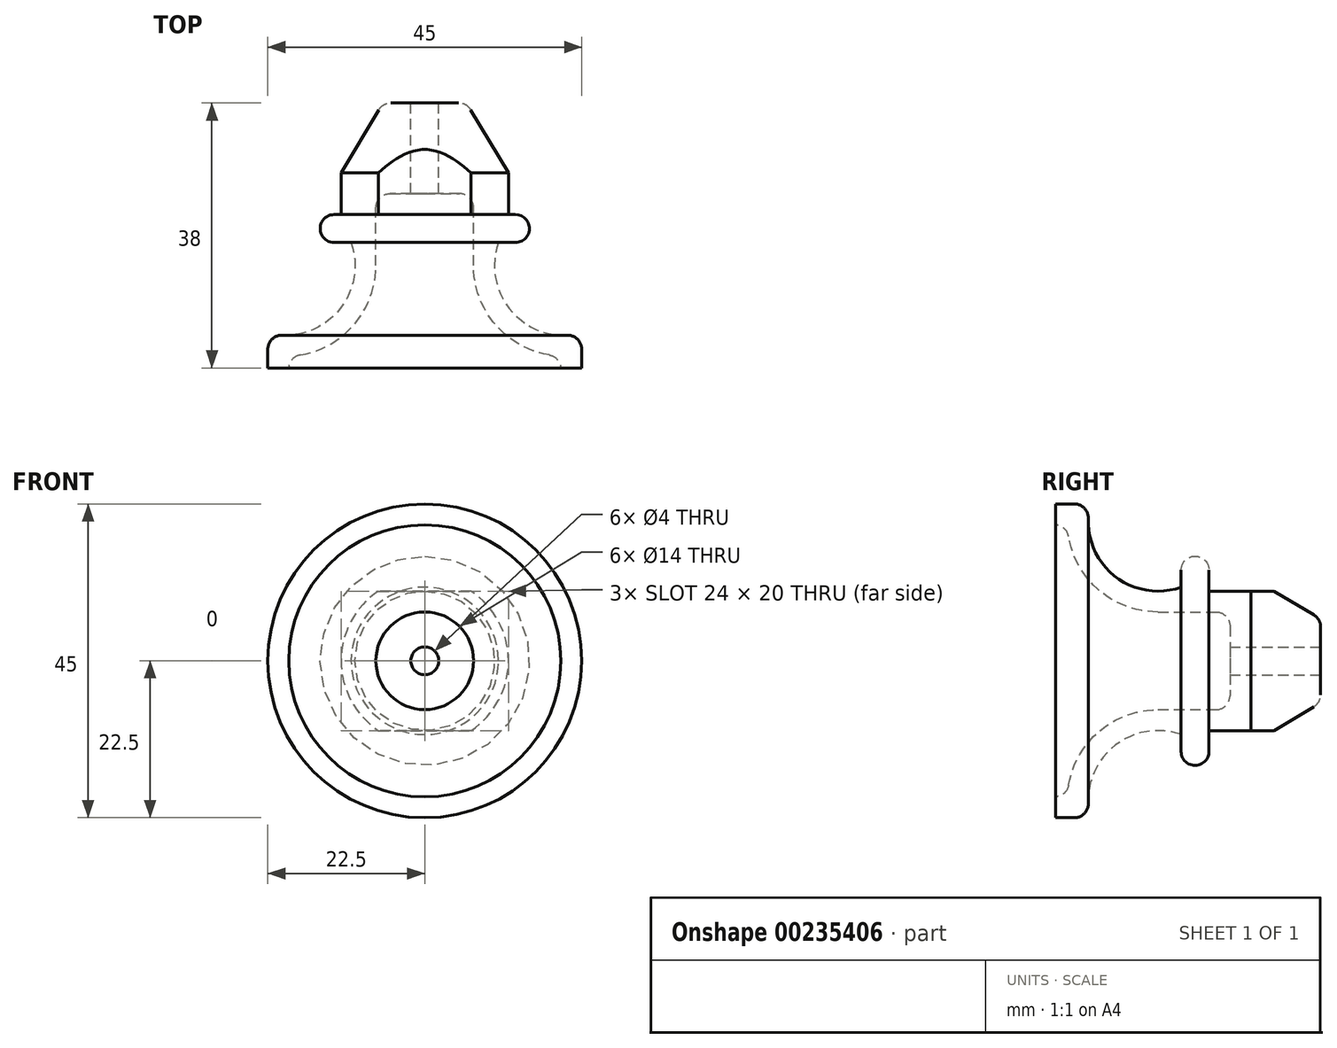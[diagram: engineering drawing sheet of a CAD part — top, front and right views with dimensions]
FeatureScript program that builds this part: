
annotation { "Feature Type Name" : "Feature", "Feature Type Description" : "" }
export const myFeature = defineFeature(function(context is Context, id is Id, definition is map)
    precondition{}
    {
        {
            var Q0;
            Q0=qCreatedBy(makeId("Top.planeOp"),FACE);
            var sketch = newSketch(context, id + "F0", { "sketchPlane" : qUnion([Q0])});
            skLineSegment(sketch, "E0", {"start": v(0, 22.95) * mm, "end": v(0, -24.97) * mm, "construction": true});
            skLineSegment(sketch, "E1", {"start": v(2, 23.32) * mm, "end": v(6, 23.32) * mm});
            skLineSegment(sketch, "E2", {"start": v(6, 23.32) * mm, "end": v(12, 13.32) * mm});
            skLineSegment(sketch, "E3", {"start": v(12, 13.32) * mm, "end": v(12, 7.32) * mm});
            skLineSegment(sketch, "E4", {"start": v(12, 7.32) * mm, "end": v(15, 7.32) * mm});
            skLineSegment(sketch, "E5", {"start": v(15, 7.32) * mm, "end": v(15, 3.32) * mm});
            skLineSegment(sketch, "E6", {"start": v(15, 3.32) * mm, "end": v(10.57, 3.32) * mm});
            skArc(sketch, "E7", {"start": v(10.57, 3.32) * mm, "mid": v(12.63, -6.76) * mm, "end": v(22.5, -9.68) * mm});
            skLineSegment(sketch, "E8", {"start": v(22.5, -9.68) * mm, "end": v(22.5, -14.68) * mm});
            skLineSegment(sketch, "E9", {"start": v(22.5, -14.68) * mm, "end": v(19.5, -14.68) * mm});
            skLineSegment(sketch, "E10", {"start": v(2, 23.32) * mm, "end": v(2, 10.32) * mm});
            skLineSegment(sketch, "E11", {"start": v(2, 10.32) * mm, "end": v(7, 10.32) * mm});
            skLineSegment(sketch, "E12", {"start": v(7, 10.32) * mm, "end": v(7, 0) * mm});
            skArc(sketch, "E13.0", {"start": v(7, 0) * mm, "mid": v(10.63, -9.01) * mm, "end": v(19.5, -13) * mm});
            skLineSegment(sketch, "E14", {"start": v(19.5, -14.68) * mm, "end": v(19.5, -13) * mm});
            skLineSegment(sketch, "E15", {"start": v(0, 19.6) * mm, "end": v(0, 22.21) * mm, "construction": true});
            skLineSegment(sketch, "E16", {"start": v(0, 22.21) * mm, "end": v(0, 27.48) * mm, "construction": true});
            skLineSegment(sketch, "E17", {"start": v(0, -27.76) * mm, "end": v(0, 35.57) * mm, "construction": true});
            skSolve(sketch);
        }
        {
            var Q0;
            Q0 = qSketchRegion(id + "F0", true);
            var Q1;
            Q1=sQuery(id+"F0.wireOp",EDGE,"E0");
            revolve(context, id + "F1", {"entities" : qUnion([Q0]), "axis" : qUnion([Q1]), "revolveType" : RevolveType.FULL});
        }
        {
            var Q0;
            Q0=makeQuery(id+"F1.opRevolve","SWEPT_EDGE",EDGE,{"disambiguationData":[OSD([sQuery(id+"F0.wireOp",EDGE,"E13.0"),sQuery(id+"F0.wireOp",EDGE,"E14")])]});
            var Q1;
            Q1=makeQuery(id+"F1.opRevolve","SWEPT_EDGE",EDGE,{"disambiguationData":[OSD([sQuery(id+"F0.wireOp",EDGE,"E11"),sQuery(id+"F0.wireOp",EDGE,"E12")])]});
            var Q2;
            Q2=makeQuery(id+"F1.opRevolve","SWEPT_EDGE",EDGE,{"disambiguationData":[OSD([sQuery(id+"F0.wireOp",EDGE,"E1"),sQuery(id+"F0.wireOp",EDGE,"E2")])]});
            var Q3;
            Q3=makeQuery(id+"F1.opRevolve","SWEPT_EDGE",EDGE,{"disambiguationData":[OSD([sQuery(id+"F0.wireOp",EDGE,"E4"),sQuery(id+"F0.wireOp",EDGE,"E5")])]});
            var Q4;
            Q4=makeQuery(id+"F1.opRevolve","SWEPT_EDGE",EDGE,{"disambiguationData":[OSD([sQuery(id+"F0.wireOp",EDGE,"E5"),sQuery(id+"F0.wireOp",EDGE,"E6")])]});
            var Q5;
            Q5=makeQuery(id+"F1.opRevolve","SWEPT_EDGE",EDGE,{"disambiguationData":[OSD([sQuery(id+"F0.wireOp",EDGE,"E7"),sQuery(id+"F0.wireOp",EDGE,"E8")])]});
            fillet(context, id + "F2", {"entities" : qUnion([Q0, Q1, Q2, Q3, Q4, Q5]), "radius" : 2 * mm, "tangentPropagation" : true, "allowEdgeOverflow" : false});
        }
        {
            var Q0;
            Q0=makeQuery(id+"F1.opRevolve","SWEPT_FACE",FACE,{"disambiguationData":[OSD([sQuery(id+"F0.wireOp",EDGE,"E4")])]});
            var sketch = newSketch(context, id + "F3", { "sketchPlane" : qUnion([Q0])});
            skCircle(sketch, "E18.0", {"center": v(0, 0) * mm, "radius": 12 * mm});
            skLineSegment(sketch, "E19.bottom", {"start": v(-6.63, 10) * mm, "end": v(6.63, 10) * mm});
            skLineSegment(sketch, "E19.top", {"start": v(-6.63, -10) * mm, "end": v(6.63, -10) * mm});
            skLineSegment(sketch, "E19.left", {"start": v(-6.63, 10) * mm, "end": v(-6.63, -10) * mm});
            skLineSegment(sketch, "E19.right", {"start": v(6.63, 10) * mm, "end": v(6.63, -10) * mm});
            skSolve(sketch);
        }
        {
            var Q0;
            {var subQ0=sQuery(id+"F3.wireOp",EDGE,"E19.bottom");Q0=makeQuery(id+"F3.imprint","IMPRINT",FACE,{"disambiguationData":[TD([[makeQuery(id+"F3.imprint","IMPRINT",EDGE,{"derivedFrom":subQ0}),1.0]])]});}
            var Q1;
            {var subQ0=sQuery(id+"F3.wireOp",EDGE,"E19.top");Q1=makeQuery(id+"F3.imprint","IMPRINT",FACE,{"disambiguationData":[TD([[makeQuery(id+"F3.imprint","IMPRINT",EDGE,{"derivedFrom":subQ0}),-1.0]])]});}
            extrude(context, id + "F4", {"entities" : qUnion([Q0, Q1]), "operationType" : NewBodyOperationType.REMOVE, "endBound" : BoundingType.THROUGH_ALL, "depth" : 25 * mm});
        }
    });
